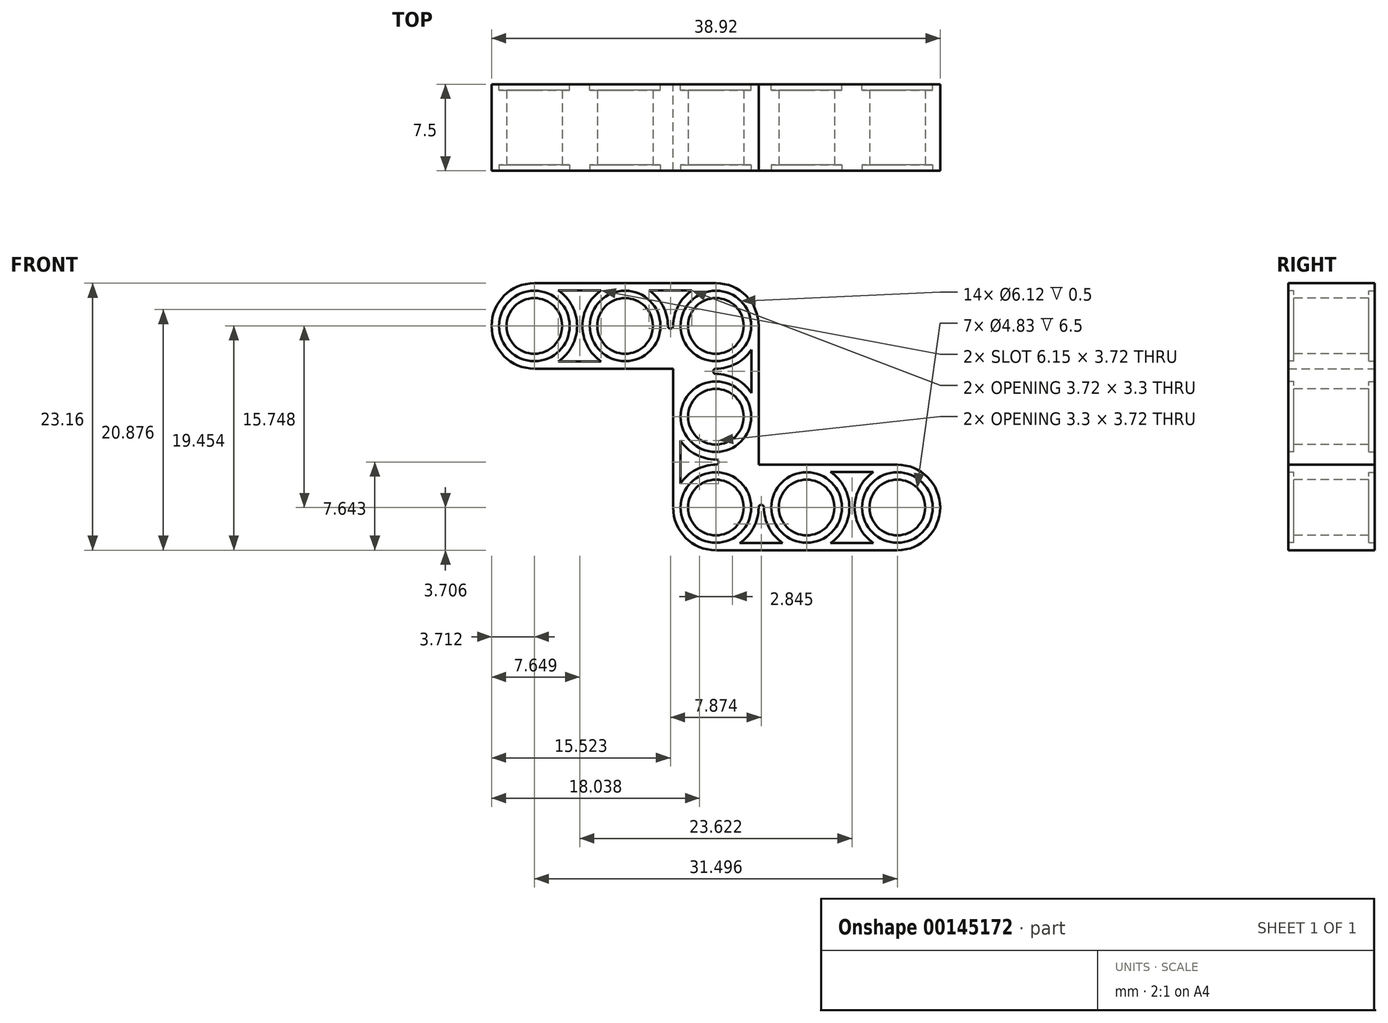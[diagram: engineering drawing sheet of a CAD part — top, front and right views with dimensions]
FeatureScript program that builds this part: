
annotation { "Feature Type Name" : "Feature", "Feature Type Description" : "" }
export const myFeature = defineFeature(function(context is Context, id is Id, definition is map)
    precondition{}
    {
        {
            var Q0;
            Q0=qCreatedBy(makeId("Front.planeOp"),FACE);
            var sketch = newSketch(context, id + "F0", { "sketchPlane" : qUnion([Q0])});
            skLineSegment(sketch, "E0", {"start": v(-19.46, 11.58) * mm, "end": v(3.7, 11.58) * mm});
            skLineSegment(sketch, "E1", {"start": v(3.7, 11.58) * mm, "end": v(3.7, -4.17) * mm});
            skLineSegment(sketch, "E2", {"start": v(3.7, -4.17) * mm, "end": v(19.46, -4.17) * mm});
            skLineSegment(sketch, "E3", {"start": v(19.46, -4.17) * mm, "end": v(19.46, -11.58) * mm});
            skLineSegment(sketch, "E4", {"start": v(19.46, -11.58) * mm, "end": v(-3.7, -11.58) * mm});
            skLineSegment(sketch, "E5", {"start": v(-3.7, -11.58) * mm, "end": v(-3.7, 4.17) * mm});
            skLineSegment(sketch, "E6", {"start": v(-3.7, 4.17) * mm, "end": v(-19.46, 4.17) * mm});
            skLineSegment(sketch, "E7", {"start": v(-19.46, 4.17) * mm, "end": v(-19.46, 11.58) * mm});
            skLineSegment(sketch, "E8", {"start": v(-3.7, 4.17) * mm, "end": v(3.7, -4.17) * mm, "construction": true});
            skLineSegment(sketch, "E9", {"start": v(0, 7.87) * mm, "end": v(0, -7.87) * mm, "construction": true});
            skLineSegment(sketch, "E10", {"start": v(-3.7, 4.17) * mm, "end": v(3.7, 11.58) * mm, "construction": true});
            skLineSegment(sketch, "E11", {"start": v(3.7, -4.17) * mm, "end": v(-3.7, -11.58) * mm, "construction": true});
            skSolve(sketch);
        }
        {
            var Q0;
            Q0=makeQuery(id+"F0.imprint","IMPRINT",FACE,{"disambiguationData":[TD([[makeQuery(id+"F0.imprint","IMPRINT",EDGE,{"derivedFrom":sQuery(id+"F0.wireOp",EDGE,"E0")}),-1.0]])]});
            extrude(context, id + "F1", {"entities" : qUnion([Q0]), "depth" : (7.5 / 2) * mm});
        }
        {
            var Q0;
            Q0=makeQuery(id+"F1.opExtrude","SWEPT_EDGE",EDGE,{"disambiguationData":[OSD([sQuery(id+"F0.wireOp",EDGE,"E0"),sQuery(id+"F0.wireOp",EDGE,"E7")])]});
            var Q1;
            Q1=makeQuery(id+"F1.opExtrude","SWEPT_EDGE",EDGE,{"disambiguationData":[OSD([sQuery(id+"F0.wireOp",EDGE,"E0"),sQuery(id+"F0.wireOp",EDGE,"E1")])]});
            var Q2;
            Q2=makeQuery(id+"F1.opExtrude","SWEPT_EDGE",EDGE,{"disambiguationData":[OSD([sQuery(id+"F0.wireOp",EDGE,"E2"),sQuery(id+"F0.wireOp",EDGE,"E3")])]});
            var Q3;
            Q3=makeQuery(id+"F1.opExtrude","SWEPT_EDGE",EDGE,{"disambiguationData":[OSD([sQuery(id+"F0.wireOp",EDGE,"E3"),sQuery(id+"F0.wireOp",EDGE,"E4")])]});
            var Q4;
            Q4=makeQuery(id+"F1.opExtrude","SWEPT_EDGE",EDGE,{"disambiguationData":[OSD([sQuery(id+"F0.wireOp",EDGE,"E4"),sQuery(id+"F0.wireOp",EDGE,"E5")])]});
            var Q5;
            Q5=makeQuery(id+"F1.opExtrude","SWEPT_EDGE",EDGE,{"disambiguationData":[OSD([sQuery(id+"F0.wireOp",EDGE,"E6"),sQuery(id+"F0.wireOp",EDGE,"E7")])]});
            fillet(context, id + "F2", {"entities" : qUnion([Q0, Q1, Q2, Q3, Q4, Q5]), "radius" : 3.7 * mm, "tangentPropagation" : true, "allowEdgeOverflow" : false});
        }
        {
            var Q0;
            Q0=makeQuery(id+"F1.opExtrude","CAP_FACE",FACE,{"disambiguationData":[OSD([sQuery(id+"F0.wireOp",EDGE,"E0"),sQuery(id+"F0.wireOp",EDGE,"E1"),sQuery(id+"F0.wireOp",EDGE,"E2"),sQuery(id+"F0.wireOp",EDGE,"E3"),sQuery(id+"F0.wireOp",EDGE,"E4"),sQuery(id+"F0.wireOp",EDGE,"E5"),sQuery(id+"F0.wireOp",EDGE,"E6"),sQuery(id+"F0.wireOp",EDGE,"E7")])],"isStart":false});
            var sketch = newSketch(context, id + "F3", { "sketchPlane" : qUnion([Q0])});
            skLineSegment(sketch, "E12", {"start": v(-13.67, 10.95) * mm, "end": v(-9.95, 10.95) * mm});
            skLineSegment(sketch, "E13", {"start": v(-13.67, 4.8) * mm, "end": v(-9.95, 4.8) * mm});
            skLineSegment(sketch, "E14", {"start": v(-5.8, 10.95) * mm, "end": v(-2.08, 10.95) * mm});
            skLineSegment(sketch, "E15", {"start": v(3.07, 5.8) * mm, "end": v(3.07, 2.08) * mm});
            skLineSegment(sketch, "E16", {"start": v(-3.07, -2.08) * mm, "end": v(-3.07, -5.8) * mm});
            skLineSegment(sketch, "E17", {"start": v(2.08, -10.95) * mm, "end": v(5.8, -10.95) * mm});
            skLineSegment(sketch, "E18", {"start": v(9.95, -10.95) * mm, "end": v(13.67, -10.95) * mm});
            skLineSegment(sketch, "E19", {"start": v(13.67, -4.8) * mm, "end": v(9.95, -4.8) * mm});
            skArc(sketch, "E20", {"start": v(13.67, -4.8) * mm, "mid": v(12.04, -7.87) * mm, "end": v(13.67, -10.95) * mm});
            skArc(sketch, "E21", {"start": v(9.95, -10.95) * mm, "mid": v(11.58, -7.87) * mm, "end": v(9.95, -4.8) * mm});
            skArc(sketch, "E22", {"start": v(4.17, -7.87) * mm, "mid": v(4.6, -9.61) * mm, "end": v(5.8, -10.95) * mm});
            skArc(sketch, "E23", {"start": v(2.08, -10.95) * mm, "mid": v(3.27, -9.61) * mm, "end": v(3.7, -7.87) * mm});
            skArc(sketch, "E24", {"start": v(0, -4.17) * mm, "mid": v(-1.74, -4.6) * mm, "end": v(-3.07, -5.8) * mm});
            skArc(sketch, "E25", {"start": v(-3.07, -2.08) * mm, "mid": v(-1.74, -3.27) * mm, "end": v(0, -3.7) * mm});
            skArc(sketch, "E26", {"start": v(3.07, 2.08) * mm, "mid": v(1.74, 3.27) * mm, "end": v(0, 3.7) * mm});
            skArc(sketch, "E27", {"start": v(0, 4.17) * mm, "mid": v(1.74, 4.6) * mm, "end": v(3.07, 5.8) * mm});
            skArc(sketch, "E28", {"start": v(-2.08, 10.95) * mm, "mid": v(-3.27, 9.61) * mm, "end": v(-3.7, 7.87) * mm});
            skArc(sketch, "E29", {"start": v(-4.17, 7.87) * mm, "mid": v(-4.6, 9.61) * mm, "end": v(-5.8, 10.95) * mm});
            skArc(sketch, "E30", {"start": v(-9.95, 10.95) * mm, "mid": v(-11.58, 7.87) * mm, "end": v(-9.95, 4.8) * mm});
            skArc(sketch, "E31", {"start": v(-13.67, 4.8) * mm, "mid": v(-12.04, 7.87) * mm, "end": v(-13.67, 10.95) * mm});
            skLineSegment(sketch, "E32", {"start": v(-15.75, 7.87) * mm, "end": v(0, 7.87) * mm, "construction": true});
            skLineSegment(sketch, "E33", {"start": v(0, -7.87) * mm, "end": v(15.75, -7.87) * mm, "construction": true});
            skArc(sketch, "E34", {"start": v(0, 4.17) * mm, "mid": v(-0.23, 3.94) * mm, "end": v(0, 3.7) * mm});
            skArc(sketch, "E35", {"start": v(-4.17, 7.87) * mm, "mid": v(-3.94, 7.65) * mm, "end": v(-3.7, 7.87) * mm});
            skArc(sketch, "E36", {"start": v(0, -4.17) * mm, "mid": v(0.23, -3.94) * mm, "end": v(0, -3.7) * mm});
            skArc(sketch, "E37", {"start": v(4.17, -7.87) * mm, "mid": v(3.94, -7.65) * mm, "end": v(3.7, -7.87) * mm});
            skSolve(sketch);
        }
        {
            var Q0;
            Q0=qSketchRegion(id+"F3",true);
            extrude(context, id + "F4", {"entities" : qUnion([Q0]), "operationType" : NewBodyOperationType.REMOVE, "oppositeDirection" : true, "depth" : 0.3 / 50.8 * mm});
        }
        {
            var Q0;
            Q0=makeQuery(id+"F1.opExtrude","CAP_FACE",FACE,{"disambiguationData":[OSD([sQuery(id+"F0.wireOp",EDGE,"E0"),sQuery(id+"F0.wireOp",EDGE,"E1"),sQuery(id+"F0.wireOp",EDGE,"E2"),sQuery(id+"F0.wireOp",EDGE,"E3"),sQuery(id+"F0.wireOp",EDGE,"E4"),sQuery(id+"F0.wireOp",EDGE,"E5"),sQuery(id+"F0.wireOp",EDGE,"E6"),sQuery(id+"F0.wireOp",EDGE,"E7")])],"isStart":false});
            var sketch = newSketch(context, id + "F5", { "sketchPlane" : qUnion([Q0])});
            skCircle(sketch, "E38", {"center": v(-15.75, 7.87) * mm, "radius": 2.41 * mm});
            skCircle(sketch, "E39", {"center": v(0, 7.87) * mm, "radius": 2.41 * mm});
            skCircle(sketch, "E40", {"center": v(0, -7.87) * mm, "radius": 2.41 * mm});
            skCircle(sketch, "E41", {"center": v(15.75, -7.87) * mm, "radius": 2.41 * mm});
            skCircle(sketch, "E42", {"center": v(-7.87, 7.87) * mm, "radius": 2.41 * mm});
            skCircle(sketch, "E43", {"center": v(0, 0) * mm, "radius": 2.41 * mm});
            skCircle(sketch, "E44", {"center": v(7.87, -7.87) * mm, "radius": 2.41 * mm});
            skLineSegment(sketch, "E45", {"start": v(-15.75, 7.87) * mm, "end": v(0, 7.87) * mm, "construction": true});
            skLineSegment(sketch, "E46", {"start": v(0, -7.87) * mm, "end": v(15.75, -7.87) * mm, "construction": true});
            skSolve(sketch);
        }
        {
            var Q0;
            Q0=qSketchRegion(id+"F5",true);
            extrude(context, id + "F6", {"entities" : qUnion([Q0]), "operationType" : NewBodyOperationType.REMOVE, "endBound" : BoundingType.UP_TO_NEXT, "oppositeDirection" : true, "depth" : 25 * mm});
        }
        {
            var Q0;
            Q0=makeQuery(id+"F1.opExtrude","CAP_FACE",FACE,{"disambiguationData":[OSD([sQuery(id+"F0.wireOp",EDGE,"E0"),sQuery(id+"F0.wireOp",EDGE,"E1"),sQuery(id+"F0.wireOp",EDGE,"E2"),sQuery(id+"F0.wireOp",EDGE,"E3"),sQuery(id+"F0.wireOp",EDGE,"E4"),sQuery(id+"F0.wireOp",EDGE,"E5"),sQuery(id+"F0.wireOp",EDGE,"E6"),sQuery(id+"F0.wireOp",EDGE,"E7")])],"isStart":false});
            var sketch = newSketch(context, id + "F7", { "sketchPlane" : qUnion([Q0])});
            skCircle(sketch, "E47", {"center": v(-15.75, 7.87) * mm, "radius": 3.06 * mm});
            skCircle(sketch, "E48", {"center": v(-7.87, 7.87) * mm, "radius": 3.06 * mm});
            skCircle(sketch, "E49", {"center": v(0, 7.87) * mm, "radius": 3.06 * mm});
            skCircle(sketch, "E50", {"center": v(0, 0) * mm, "radius": 3.06 * mm});
            skCircle(sketch, "E51", {"center": v(0, -7.87) * mm, "radius": 3.06 * mm});
            skCircle(sketch, "E52", {"center": v(7.87, -7.87) * mm, "radius": 3.06 * mm});
            skCircle(sketch, "E53", {"center": v(15.75, -7.87) * mm, "radius": 3.06 * mm});
            skLineSegment(sketch, "E54", {"start": v(-15.75, 7.87) * mm, "end": v(0, 7.87) * mm, "construction": true});
            skLineSegment(sketch, "E55", {"start": v(0, 7.87) * mm, "end": v(0, -7.87) * mm, "construction": true});
            skLineSegment(sketch, "E56", {"start": v(0, -7.87) * mm, "end": v(15.75, -7.87) * mm, "construction": true});
            skSolve(sketch);
        }
        {
            var Q0;
            Q0=qSketchRegion(id+"F7",true);
            extrude(context, id + "F8", {"entities" : qUnion([Q0]), "operationType" : NewBodyOperationType.REMOVE, "oppositeDirection" : true, "depth" : .5 * mm});
        }
        {
            var Q0;
            Q0=makeQuery(id+"F1.opExtrude","SWEPT_BODY",BODY,{"disambiguationData":[OSD([sQuery(id+"F0.wireOp",EDGE,"E0"),sQuery(id+"F0.wireOp",EDGE,"E1"),sQuery(id+"F0.wireOp",EDGE,"E2"),sQuery(id+"F0.wireOp",EDGE,"E3"),sQuery(id+"F0.wireOp",EDGE,"E4"),sQuery(id+"F0.wireOp",EDGE,"E5"),sQuery(id+"F0.wireOp",EDGE,"E6"),sQuery(id+"F0.wireOp",EDGE,"E7")])]});
            var Q1;
            Q1=qCreatedBy(makeId("Front.planeOp"),FACE);
            mirror(context, id + "F9", {"operationType" : NewBodyOperationType.ADD, "entities" : qUnion([Q0]), "mirrorPlane" : qUnion([Q1])});
        }
    });
